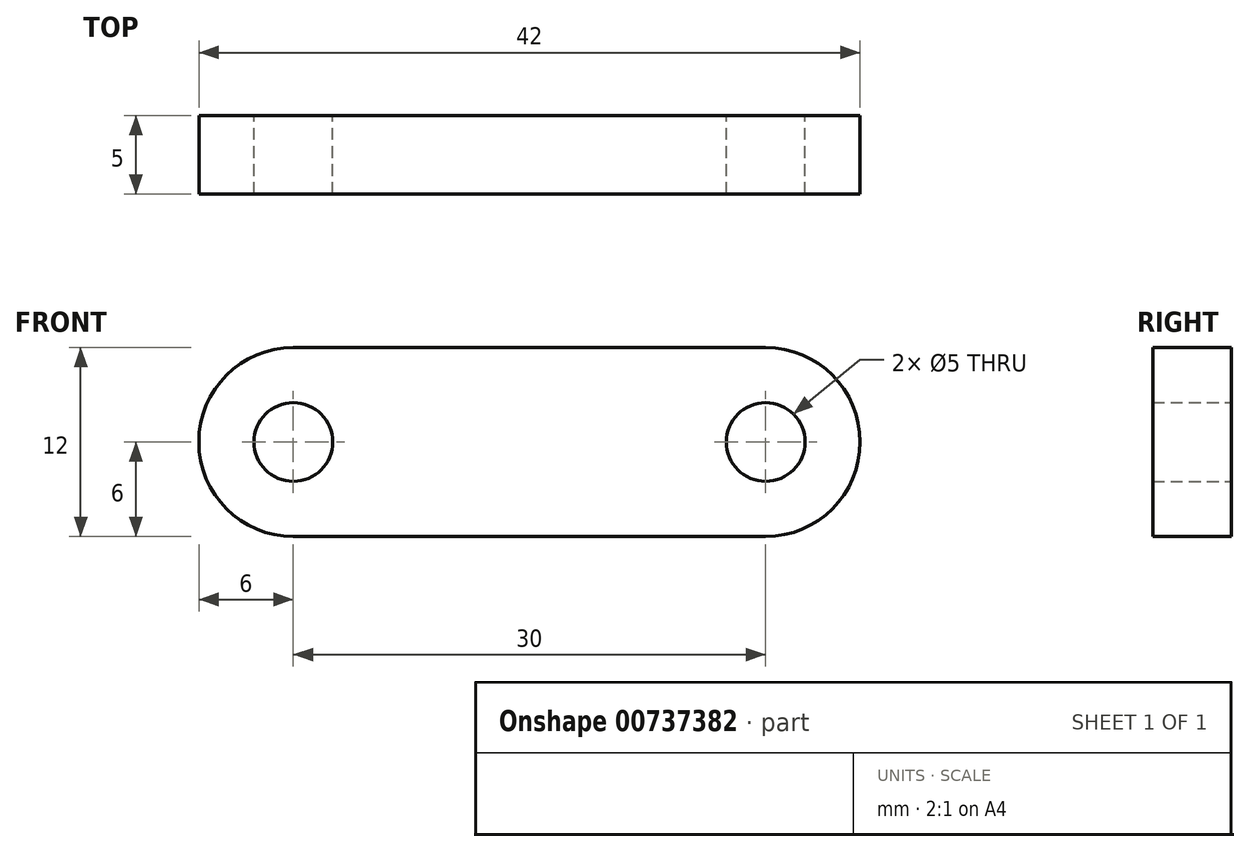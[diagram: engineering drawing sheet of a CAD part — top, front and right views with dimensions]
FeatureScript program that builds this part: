
annotation { "Feature Type Name" : "Feature", "Feature Type Description" : "" }
export const myFeature = defineFeature(function(context is Context, id is Id, definition is map)
    precondition{}
    {
        {
            var Q0;
            Q0=qCreatedBy(makeId("Front.planeOp"),FACE);
            var sketch = newSketch(context, id + "F0", { "sketchPlane" : qUnion([Q0])});
            skLineSegment(sketch, "E0.bottom", {"start": v(0, 0) * mm, "end": v(30, 0) * mm});
            skLineSegment(sketch, "E0.top", {"start": v(0, 12) * mm, "end": v(30, 12) * mm});
            skArc(sketch, "E1", {"start": v(30, 0) * mm, "mid": v(36, 6) * mm, "end": v(30, 12) * mm});
            skArc(sketch, "E2", {"start": v(0, 12) * mm, "mid": v(-6, 6) * mm, "end": v(0, 0) * mm});
            skCircle(sketch, "E3", {"center": v(0, 6) * mm, "radius": 2.5 * mm});
            skCircle(sketch, "E4", {"center": v(30, 6) * mm, "radius": 2.5 * mm});
            skSolve(sketch);
        }
        {
            var Q0;
            Q0=makeQuery(id+"F0.imprint","IMPRINT",FACE,{"disambiguationData":[TD([[makeQuery(id+"F0.imprint","IMPRINT",EDGE,{"derivedFrom":sQuery(id+"F0.wireOp",EDGE,"E0.bottom")}),1.0]])]});
            var Q1;
            Q1=makeQuery(id+"F0.imprint","IMPRINT",FACE,{"disambiguationData":[TD([[makeQuery(id+"F0.imprint","IMPRINT",EDGE,{"derivedFrom":sQuery(id+"F0.wireOp",EDGE,"G6ocFgkO-YUp3-gcwV-9g9h-jVaogv9Dnoo6")}),1.0]])]});
            var Q2;
            Q2=makeQuery(id+"F0.imprint","IMPRINT",FACE,{"disambiguationData":[TD([[makeQuery(id+"F0.imprint","IMPRINT",EDGE,{"derivedFrom":sQuery(id+"F0.wireOp",EDGE,"e4FgApFk-CMKc-RMS7-eMPg-ILMOAhxH3vV0")}),1.0]])]});
            extrude(context, id + "F1", {"entities" : qUnion([Q0, Q1, Q2]), "depth" : 5 * mm, "offsetDistance" : 25 * mm});
        }
    });
